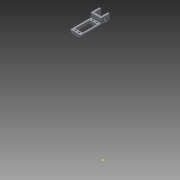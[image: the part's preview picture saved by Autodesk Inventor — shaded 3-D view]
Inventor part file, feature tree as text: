
AUTODESK INVENTOR PART (.ipt)
format: ipt  version: 2015 (Build 190159000, 159)  size: 167,936 bytes
history: native  units: in
note: dims shown in document units (in); Inventor stores cm internally (conversion verified against a paired STEP export)
features: reference x14, sketch x8, extrude x7, projected_geometry x3, plane x2, chamfer x1
ambient origin geometry x8: Origin, YZ Plane, XZ Plane, XY Plane, X Axis, Y Axis, Z Axis, Center Point
bodies: Solid1 (feature_tree)
feature tree (35):
  plane  "Work Plane1"
  plane  "Work Plane2"
  extrude  "Extrusion1"  Depth=2.4375in TaperAngle=0.0deg
  extrude  "Extrusion2"  Depth=0.75in TaperAngle=0.0deg
  extrude  "Extrusion3"  TaperAngle=180.0deg  [1 undecoded]
  extrude  "Extrusion4"  Depth=0.5in
  extrude  "Extrusion5"  Depth=0.5in TaperAngle=0.0deg
  extrude  "Extrusion6"  [1 undecoded]
  sketch  "Sketch10"
  extrude  "Extrusion7"  [1 undecoded]
  chamfer  "Chamfer1"  [1 undecoded]
  sketch  "Sketch2"  dims[d0=2.4375in d1=0.0in d2=2.4375in d3=0.0in]
  reference  "Reference1"
  reference  "Reference2"
  sketch  "Sketch3"  dims[d4=2.4375in d5=0.0in d6=0.75in d7=0.0in]
  reference  "Reference3"
  reference  "Reference4"
  reference  "Reference5"
  reference  "Reference6"
  sketch  "Sketch4"  dims[d8=0.5625in d9=0.0in d10=180.0deg]
  reference  "Reference7"
  reference  "Reference8"
  reference  "Reference9"
  reference  "Reference10"
  sketch  "Sketch6"  dims[d11=0.5in d12=0.0in d13=0.1406in]
  projected_geometry  "Projected Loop1"
  sketch  "Sketch7"  dims[d14=0.1406in d15=0.5in d16=0.0in]
  reference  "Reference13"
  reference  "Reference14"
  reference  "Reference15"
  reference  "Reference16"
  sketch  "Sketch8"  dims[d17=0.1875in d18=0.125in d19=45.0deg]
  projected_geometry  "Projected Loop2"
  sketch  "Sketch11"
  projected_geometry  "Projected Loop3"
note: 4 required parameter values undecoded (feature->parameter linkage not recoverable at this tier; creation-order binding heuristic only, values carry confidence <= 0.55)
